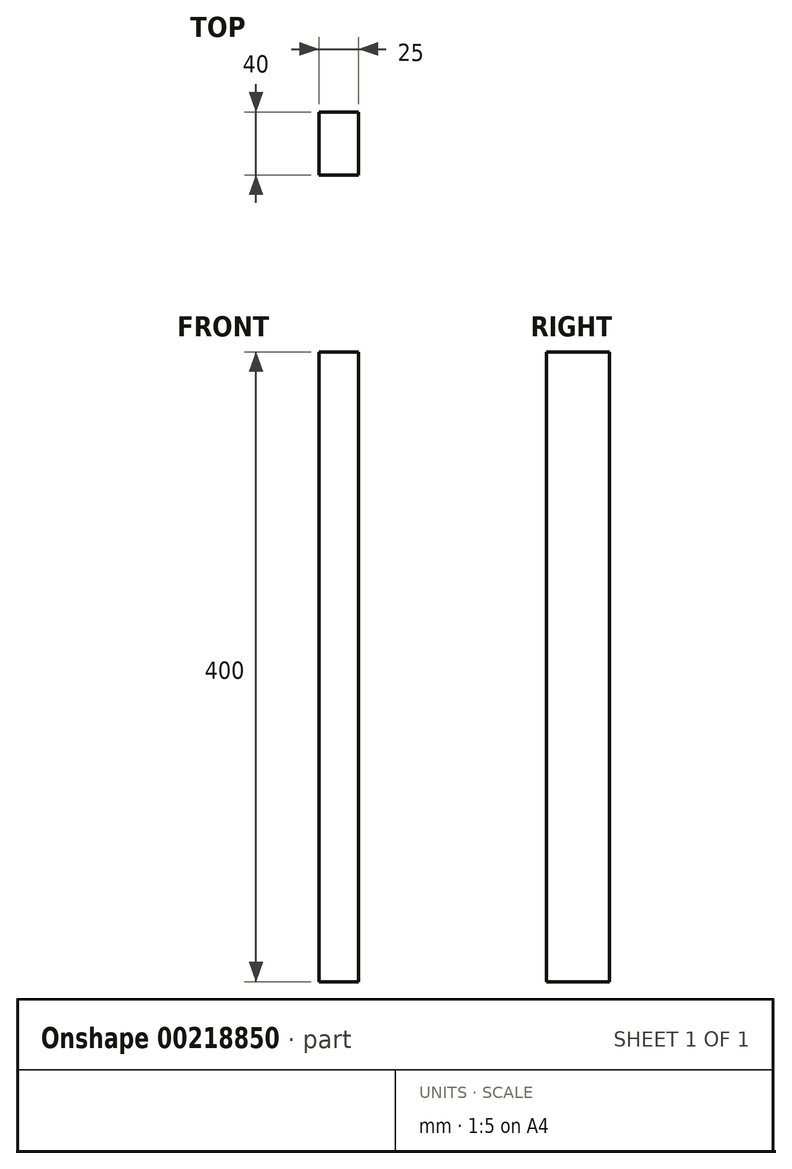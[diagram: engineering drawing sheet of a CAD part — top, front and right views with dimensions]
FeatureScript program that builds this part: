
annotation { "Feature Type Name" : "Feature", "Feature Type Description" : "" }
export const myFeature = defineFeature(function(context is Context, id is Id, definition is map)
    precondition{}
    {
        {
            var Q0;
            Q0=qCreatedBy(makeId("Right.planeOp"),FACE);
            var sketch = newSketch(context, id + "F0", { "sketchPlane" : qUnion([Q0])});
            skLineSegment(sketch, "E0.bottom", {"start": v(-40, 335.3) * mm, "end": v(0, 335.3) * mm});
            skLineSegment(sketch, "E0.top", {"start": v(-40, -64.7) * mm, "end": v(0, -64.7) * mm});
            skLineSegment(sketch, "E0.left", {"start": v(-40, 335.3) * mm, "end": v(-40, -64.7) * mm});
            skLineSegment(sketch, "E0.right", {"start": v(0, 335.3) * mm, "end": v(0, -64.7) * mm});
            skSolve(sketch);
        }
        {
            var Q0;
            Q0=makeQuery(id+"F0.imprint","IMPRINT",FACE,{"disambiguationData":[TD([[makeQuery(id+"F0.imprint","IMPRINT",EDGE,{"derivedFrom":sQuery(id+"F0.wireOp",EDGE,"E0.bottom")}),-1.0]])]});
            extrude(context, id + "F1", {"entities" : qUnion([Q0]), "depth" : 25 * mm});
        }
    });
